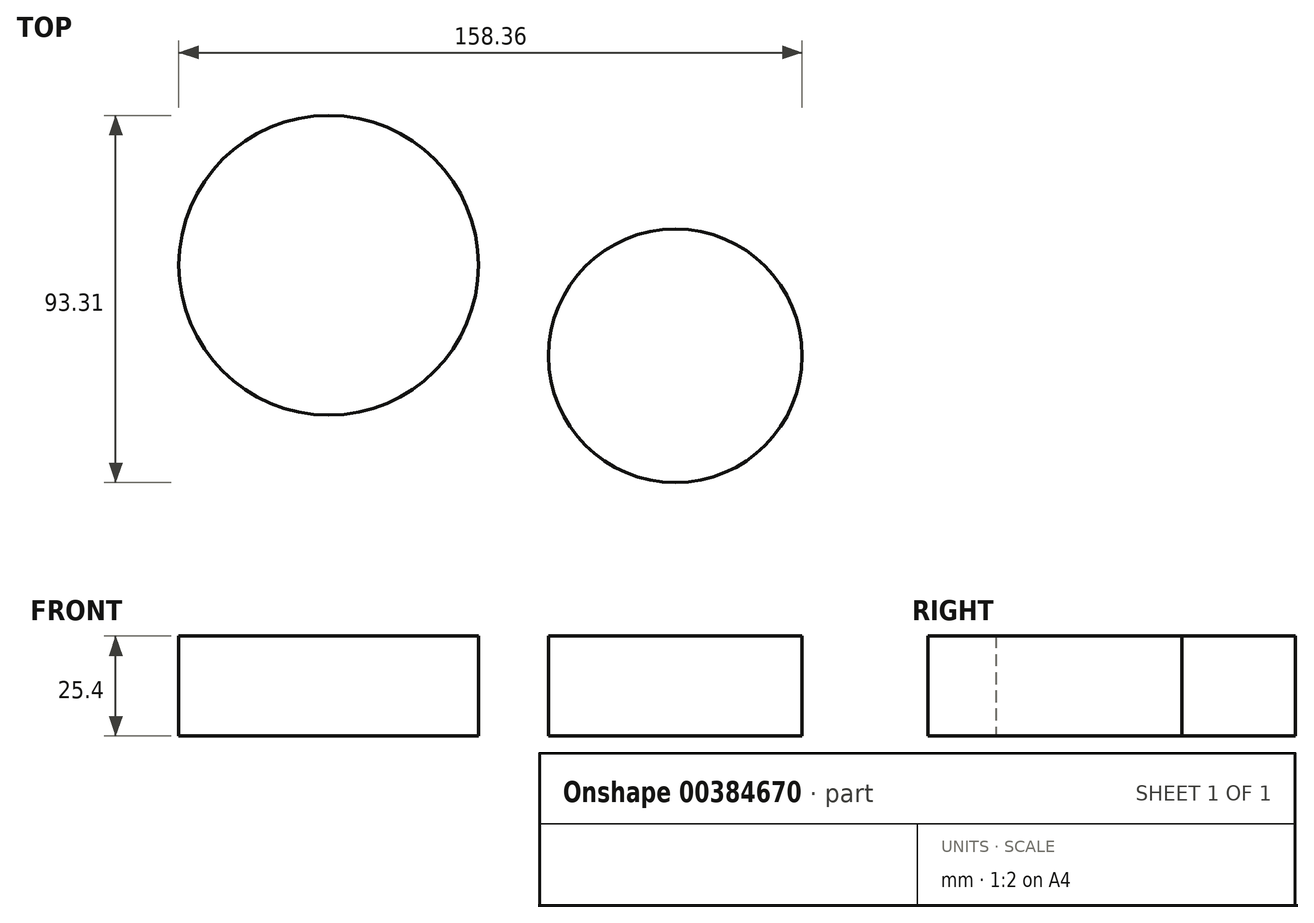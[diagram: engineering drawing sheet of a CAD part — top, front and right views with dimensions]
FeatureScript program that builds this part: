
annotation { "Feature Type Name" : "Feature", "Feature Type Description" : "" }
export const myFeature = defineFeature(function(context is Context, id is Id, definition is map)
    precondition{}
    {
        {
            var Q0;
            Q0=qCreatedBy(makeId("Top.planeOp"),FACE);
            var sketch = newSketch(context, id + "F0", { "sketchPlane" : qUnion([Q0])});
            skCircle(sketch, "E0", {"center": v(0, 0) * mm, "radius": 32.22 * mm});
            skSolve(sketch);
        }
        {
            var Q0;
            Q0 = qSketchRegion(id + "F0", true);
            extrude(context, id + "F1", {"entities" : qUnion([Q0]), "depth" : 25.4 * mm});
        }
        {
            var Q0;
            Q0=makeQuery(id+"F1.opExtrude","CAP_FACE",FACE,{"disambiguationData":[OSD([sQuery(id+"F0.wireOp",EDGE,"E0")])],"isStart":false});
            var sketch = newSketch(context, id + "F2", { "sketchPlane" : qUnion([Q0])});
            skFitSpline(sketch, "E1", {"points": [v(-13.68, 15.91) * mm, v(-19.38, 11.23) * mm, v(-15.1, 7.57) * mm, v(-9.61, 10.82) * mm, v(-13.68, 15.91) * mm]});
            skFitSpline(sketch, "E2", {"points": [v(6.46, 15.91) * mm, v(3.82, 11.43) * mm, v(8.1, 8.79) * mm, v(12.36, 12.25) * mm, v(6.46, 15.91) * mm]});
            skFitSpline(sketch, "E3", {"points": [v(-1.88, 4.3) * mm, v(-5.54, 0) * mm, v(-1.88, -5.05) * mm, v(0, -3.42) * mm, v(-1.88, 4.3) * mm]});
            skFitSpline(sketch, "E4", {"points": [v(-16.94, -10.95) * mm, v(-7.38, -21.74) * mm, v(7.68, -19.7) * mm, v(15.01, -12.78) * mm, v(12.16, -8.1) * mm, v(0, -8.3) * mm, v(-9.82, -8.3) * mm, v(-16.94, -10.95) * mm]});
            skFitSpline(sketch, "E5", {"points": [v(-22.16, 23.4) * mm, v(-23.86, 19.17) * mm, v(-29.09, 13.85) * mm, v(-27.93, 9) * mm, v(-29.15, 4.51) * mm, v(-28.54, -2.6) * mm, v(-31.18, -8.1) * mm, v(-28.13, -10.95) * mm, v(-27.12, -12.78) * mm, v(-26.7, -8.1) * mm, v(-28.13, -5.05) * mm, v(-26.7, 0) * mm, v(-26.7, 3.3) * mm, v(-26.3, 8.79) * mm, v(-25.7, 13.67) * mm, v(-23.86, 15.91) * mm, v(-20.4, 18.96) * mm, v(-15.52, 24.46) * mm, v(-11.45, 24.66) * mm, v(-8.8, 21.6) * mm, v(-13.68, 20.6) * mm, v(-6.36, 18.56) * mm, v(-1.88, 20.39) * mm, v(2.4, 21.6) * mm, v(8.3, 19.98) * mm, v(12.16, 19.57) * mm, v(9.1, 22.22) * mm, v(15.01, 20.18) * mm, v(16.64, 15.91) * mm, v(18.67, 11.43) * mm, v(21.52, 5.33) * mm, v(23.35, -1.8) * mm, v(25.39, -10.95) * mm, v(31.18, -8.1) * mm, v(32.18, -1.66) * mm, v(29.87, 4.1) * mm, v(25.6, 15.91) * mm, v(24.78, 20.6) * mm, v(17.05, 24.46) * mm, v(12.16, 27.51) * mm, v(9.32, 30.84) * mm, v(-1.88, 29.75) * mm, v(-5.52, 31.74) * mm, v(-10.63, 28.32) * mm, v(-13.68, 26.5) * mm, v(-16.94, 27.4) * mm, v(-22.16, 23.4) * mm]});
            skSolve(sketch);
        }
        {
            var Q0;
            Q0=qCreatedBy(makeId("Top.planeOp"),FACE);
            var sketch = newSketch(context, id + "F3", { "sketchPlane" : qUnion([Q0])});
            skCircle(sketch, "E6", {"center": v(-88.07, 23.02) * mm, "radius": 38.07 * mm});
            skSolve(sketch);
        }
        {
            var Q0;
            Q0 = qSketchRegion(id + "F3", true);
            extrude(context, id + "F4", {"entities" : qUnion([Q0]), "depth" : 25.4 * mm});
        }
    });
